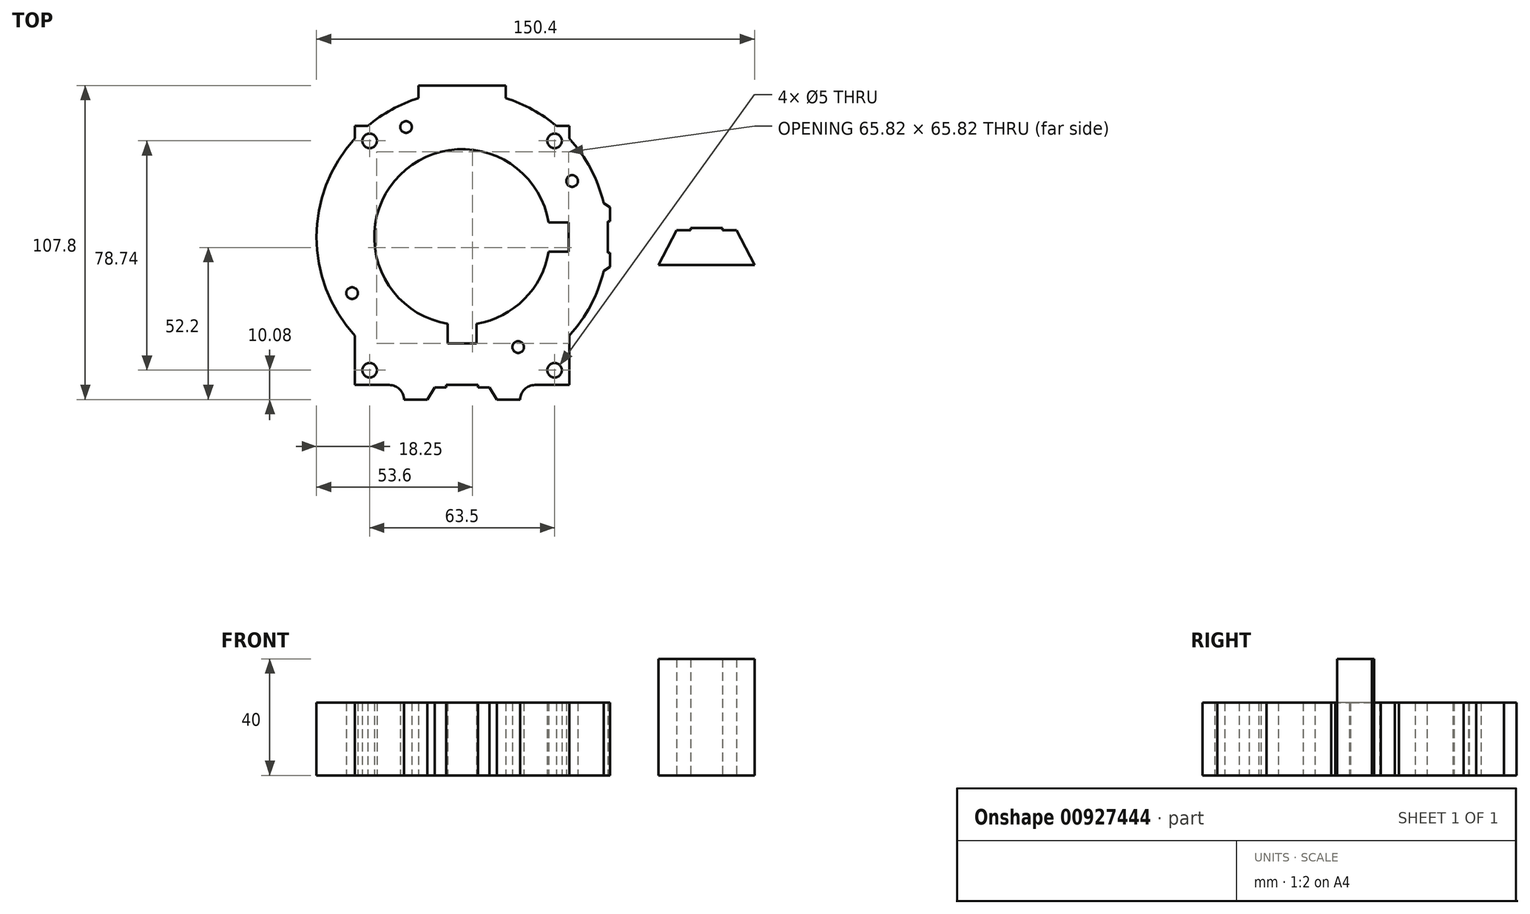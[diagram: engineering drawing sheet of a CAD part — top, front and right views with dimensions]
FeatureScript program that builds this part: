
annotation { "Feature Type Name" : "Feature", "Feature Type Description" : "" }
export const myFeature = defineFeature(function(context is Context, id is Id, definition is map)
    precondition{}
    {
        {
            var Q0;
            Q0=qCreatedBy(makeId("Top.planeOp"),FACE);
            var sketch = newSketch(context, id + "F0", { "sketchPlane" : qUnion([Q0])});
            skArc(sketch, "E0", {"start": v(36.83, -33.82) * mm, "mid": v(44.15, -23.47) * mm, "end": v(48.63, -11.6) * mm});
            skArc(sketch, "E1", {"start": v(5, -29.75) * mm, "mid": v(21.33, -21.33) * mm, "end": v(29.75, -5) * mm});
            skLineSegment(sketch, "E2.bottom", {"start": v(36.83, -50.8) * mm, "end": v(24.97, -50.8) * mm});
            skLineSegment(sketch, "E2.top", {"start": v(36.83, 38.1) * mm, "end": v(32.38, 38.1) * mm});
            skLineSegment(sketch, "E2.right", {"start": v(-36.83, -50.8) * mm, "end": v(-36.83, -33.82) * mm});
            skPoint(sketch, "E2.middle", {"position": v(0, -6.35) * mm});
            skLineSegment(sketch, "E3", {"start": v(0, 0) * mm, "end": v(37.78, 19.25) * mm, "construction": true});
            skCircle(sketch, "E4", {"center": v(37.78, 19.25) * mm, "radius": 2 * mm});
            skLineSegment(sketch, "E5.bottom", {"start": v(-36.83, -50.8) * mm, "end": v(-31.75, -50.8) * mm, "construction": true});
            skLineSegment(sketch, "E5.top", {"start": v(-36.83, -45.72) * mm, "end": v(-31.75, -45.72) * mm, "construction": true});
            skLineSegment(sketch, "E5.left", {"start": v(-36.83, -50.8) * mm, "end": v(-36.83, -45.72) * mm, "construction": true});
            skLineSegment(sketch, "E5.right", {"start": v(-31.75, -50.8) * mm, "end": v(-31.75, -45.72) * mm, "construction": true});
            skLineSegment(sketch, "E6", {"start": v(0, -6.35) * mm, "end": v(11.23, -6.35) * mm, "construction": true});
            skLineSegment(sketch, "E7", {"start": v(36.83, 38.1) * mm, "end": v(36.83, 33.82) * mm});
            skArc(sketch, "E8.trimOffspring", {"start": v(32.38, 38.1) * mm, "mid": v(24.17, 43.77) * mm, "end": v(15, 47.7) * mm});
            skLineSegment(sketch, "E9.trimOffspring", {"start": v(-32.38, 38.1) * mm, "end": v(-36.83, 38.1) * mm});
            skArc(sketch, "E10.trimOffspring", {"start": v(-36.83, 33.82) * mm, "mid": v(-50, 0) * mm, "end": v(-36.83, -33.82) * mm});
            skLineSegment(sketch, "E11.trimOffspring", {"start": v(-36.83, 33.82) * mm, "end": v(-36.83, 38.1) * mm});
            skLineSegment(sketch, "E12", {"start": v(-36.83, 33.82) * mm, "end": v(-36.83, -33.82) * mm, "construction": true});
            skLineSegment(sketch, "E13", {"start": v(36.83, -33.82) * mm, "end": v(36.83, 33.82) * mm, "construction": true});
            skLineSegment(sketch, "E14", {"start": v(32.38, 38.1) * mm, "end": v(-32.38, 38.1) * mm, "construction": true});
            skCircle(sketch, "E15", {"center": v(37.78, 19.25) * mm, "radius": 4 * mm, "construction": true});
            skLineSegment(sketch, "E16", {"start": v(3.2, -36.51) * mm, "end": v(3.2, -50.8) * mm, "construction": true});
            skLineSegment(sketch, "E17.MirrorCS", {"start": v(-3.2, -36.51) * mm, "end": v(-3.2, -50.8) * mm, "construction": true});
            skLineSegment(sketch, "E18", {"start": v(36.83, -50.8) * mm, "end": v(36.83, -33.82) * mm});
            skLineSegment(sketch, "E19", {"start": v(83.9, -9.58) * mm, "end": v(100.4, -9.58) * mm});
            skLineSegment(sketch, "E20", {"start": v(83.9, 3.12) * mm, "end": v(89.35, 3.12) * mm});
            skLineSegment(sketch, "E21", {"start": v(89.35, 3.12) * mm, "end": v(89.35, 2.32) * mm});
            skLineSegment(sketch, "E22", {"start": v(89.35, 2.32) * mm, "end": v(94.18, 2.32) * mm});
            skLineSegment(sketch, "E23", {"start": v(100.4, -9.58) * mm, "end": v(94.18, 2.32) * mm});
            skLineSegment(sketch, "E24.MirrorCS", {"start": v(78.46, 3.12) * mm, "end": v(78.46, 2.32) * mm});
            skLineSegment(sketch, "E25.MirrorCS", {"start": v(78.46, 2.32) * mm, "end": v(73.63, 2.32) * mm});
            skLineSegment(sketch, "E26.MirrorCS", {"start": v(67.4, -9.58) * mm, "end": v(73.63, 2.32) * mm});
            skLineSegment(sketch, "E27.MirrorCS", {"start": v(83.9, -9.58) * mm, "end": v(67.4, -9.58) * mm});
            skLineSegment(sketch, "E28.MirrorCS", {"start": v(83.9, 3.12) * mm, "end": v(78.46, 3.12) * mm});
            skLineSegment(sketch, "E29", {"start": v(0, -50.8) * mm, "end": v(5.44, -50.8) * mm, "construction": true});
            skLineSegment(sketch, "E30", {"start": v(5.44, -50.8) * mm, "end": v(5.44, -51.6) * mm});
            skLineSegment(sketch, "E31", {"start": v(5.44, -51.6) * mm, "end": v(9.45, -51.6) * mm});
            skLineSegment(sketch, "E32", {"start": v(9.45, -51.6) * mm, "end": v(11.97, -55.8) * mm});
            skLineSegment(sketch, "E33", {"start": v(11.97, -55.8) * mm, "end": v(19.97, -55.8) * mm});
            skLineSegment(sketch, "E34", {"start": v(19.97, -55.8) * mm, "end": v(24.97, -55.8) * mm, "construction": true});
            skArc(sketch, "E35", {"start": v(19.97, -55.8) * mm, "mid": v(21.43, -52.26) * mm, "end": v(24.97, -50.8) * mm});
            skLineSegment(sketch, "E36.MirrorCS", {"start": v(-5.44, -50.8) * mm, "end": v(-5.44, -51.6) * mm});
            skLineSegment(sketch, "E37.MirrorCS", {"start": v(-5.44, -51.6) * mm, "end": v(-9.45, -51.6) * mm});
            skLineSegment(sketch, "E38.MirrorCS", {"start": v(-19.97, -55.8) * mm, "end": v(-24.97, -55.8) * mm, "construction": true});
            skLineSegment(sketch, "E39.MirrorCS", {"start": v(-9.45, -51.6) * mm, "end": v(-11.97, -55.8) * mm});
            skArc(sketch, "E40.MirrorCS", {"start": v(-19.97, -55.8) * mm, "mid": v(-21.43, -52.26) * mm, "end": v(-24.97, -50.8) * mm});
            skLineSegment(sketch, "E41.MirrorCS", {"start": v(-11.97, -55.8) * mm, "end": v(-19.97, -55.8) * mm});
            skLineSegment(sketch, "E42.trimOffspring", {"start": v(-24.97, -50.8) * mm, "end": v(-36.83, -50.8) * mm});
            skLineSegment(sketch, "E43.trimOffspring", {"start": v(5.44, -50.8) * mm, "end": v(-5.44, -50.8) * mm});
            skLineSegment(sketch, "E44", {"start": v(-24.97, -50.8) * mm, "end": v(-5.44, -50.8) * mm, "construction": true});
            skLineSegment(sketch, "E45", {"start": v(5.44, -50.8) * mm, "end": v(24.97, -50.8) * mm, "construction": true});
            skLineSegment(sketch, "E46", {"start": v(50, 0) * mm, "end": v(50, 5.45) * mm});
            skLineSegment(sketch, "E47", {"start": v(50, 5.45) * mm, "end": v(50.8, 5.45) * mm});
            skLineSegment(sketch, "E48", {"start": v(50.8, 5.45) * mm, "end": v(50.8, 10.28) * mm});
            skLineSegment(sketch, "E49", {"start": v(50.8, 10.28) * mm, "end": v(48.63, 11.6) * mm});
            skLineSegment(sketch, "E50.MirrorCS", {"start": v(50, 0) * mm, "end": v(50, -5.45) * mm});
            skLineSegment(sketch, "E51.MirrorCS", {"start": v(50, -5.45) * mm, "end": v(50.8, -5.45) * mm});
            skLineSegment(sketch, "E52.MirrorCS", {"start": v(50.8, -5.45) * mm, "end": v(50.8, -10.28) * mm});
            skLineSegment(sketch, "E53.MirrorCS", {"start": v(50.8, -10.28) * mm, "end": v(48.63, -11.6) * mm});
            skArc(sketch, "E54.trimOffspring", {"start": v(48.63, 11.6) * mm, "mid": v(44.15, 23.47) * mm, "end": v(36.83, 33.82) * mm});
            skArc(sketch, "E55", {"start": v(48.63, 11.6) * mm, "mid": v(50, 0) * mm, "end": v(48.63, -11.6) * mm, "construction": true});
            skLineSegment(sketch, "E56", {"start": v(0, 50) * mm, "end": v(0, 52) * mm, "construction": true});
            skLineSegment(sketch, "E57", {"start": v(0, 52) * mm, "end": v(15, 52) * mm});
            skLineSegment(sketch, "E58", {"start": v(15, 52) * mm, "end": v(15, 47.7) * mm});
            skLineSegment(sketch, "E59.MirrorCS", {"start": v(0, 52) * mm, "end": v(-15, 52) * mm});
            skLineSegment(sketch, "E60.MirrorCS", {"start": v(-15, 52) * mm, "end": v(-15, 47.7) * mm});
            skArc(sketch, "E61.trimOffspring", {"start": v(-15, 47.7) * mm, "mid": v(-24.17, 43.77) * mm, "end": v(-32.38, 38.1) * mm});
            skArc(sketch, "E62", {"start": v(-15, 47.7) * mm, "mid": v(0, 50) * mm, "end": v(15, 47.7) * mm, "construction": true});
            skLineSegment(sketch, "E63", {"start": v(0, -36.51) * mm, "end": v(5, -36.51) * mm});
            skLineSegment(sketch, "E64", {"start": v(5, -36.51) * mm, "end": v(5, -29.75) * mm});
            skLineSegment(sketch, "E65.MirrorCS", {"start": v(-5, -36.51) * mm, "end": v(-5, -29.75) * mm});
            skLineSegment(sketch, "E66.MirrorCS", {"start": v(0, -36.51) * mm, "end": v(-5, -36.51) * mm});
            skArc(sketch, "E67.MirrorC", {"start": v(-5, -29.75) * mm, "mid": v(-21.33, 21.33) * mm, "end": v(29.75, 5) * mm});
            skArc(sketch, "E68", {"start": v(-5, -29.75) * mm, "mid": v(0, -30.16) * mm, "end": v(5, -29.75) * mm, "construction": true});
            skLineSegment(sketch, "E69.1.0", {"start": v(36.51, 0) * mm, "end": v(36.51, -5) * mm});
            skLineSegment(sketch, "E69.1.1", {"start": v(36.51, 0) * mm, "end": v(36.51, 5) * mm});
            skLineSegment(sketch, "E69.1.2", {"start": v(36.51, 5) * mm, "end": v(29.75, 5) * mm});
            skLineSegment(sketch, "E69.1.3", {"start": v(36.51, -5) * mm, "end": v(29.75, -5) * mm});
            skArc(sketch, "E70.trimOffspring", {"start": v(29.75, -5) * mm, "mid": v(21.33, -21.33) * mm, "end": v(5, -29.75) * mm});
            skArc(sketch, "E71.trimOffspring", {"start": v(29.75, 5) * mm, "mid": v(-21.33, 21.33) * mm, "end": v(-5, -29.75) * mm, "construction": true});
            skArc(sketch, "E72", {"start": v(29.75, -5) * mm, "mid": v(30.16, 0) * mm, "end": v(29.75, 5) * mm, "construction": true});
            skArc(sketch, "E73", {"start": v(-36.83, -33.82) * mm, "mid": v(0, -50) * mm, "end": v(36.83, -33.82) * mm, "construction": true});
            skCircle(sketch, "E74", {"center": v(-31.75, -45.72) * mm, "radius": 2.5 * mm});
            skCircle(sketch, "E75", {"center": v(-31.75, -45.72) * mm, "radius": 3.2 * mm, "construction": true});
            skCircle(sketch, "E76.MirrorC", {"center": v(31.75, -45.72) * mm, "radius": 3.2 * mm, "construction": true});
            skCircle(sketch, "E77.MirrorC", {"center": v(31.75, -45.72) * mm, "radius": 2.5 * mm});
            skCircle(sketch, "E78.MirrorC", {"center": v(31.75, 33.02) * mm, "radius": 3.2 * mm, "construction": true});
            skCircle(sketch, "E79.MirrorC", {"center": v(31.75, 33.02) * mm, "radius": 2.5 * mm});
            skCircle(sketch, "E80.MirrorC", {"center": v(-31.75, 33.02) * mm, "radius": 3.2 * mm, "construction": true});
            skCircle(sketch, "E81.MirrorC", {"center": v(-31.75, 33.02) * mm, "radius": 2.5 * mm});
            skCircle(sketch, "E82", {"center": v(37.78, 19.25) * mm, "radius": 5 * mm, "construction": true});
            skCircle(sketch, "E83", {"center": v(37.78, 19.25) * mm, "radius": 3.5 * mm, "construction": true});
            skCircle(sketch, "E84.1.0", {"center": v(-19.25, 37.78) * mm, "radius": 2 * mm});
            skCircle(sketch, "E84.1.1", {"center": v(-19.25, 37.78) * mm, "radius": 3.5 * mm, "construction": true});
            skCircle(sketch, "E84.1.2", {"center": v(-19.25, 37.78) * mm, "radius": 4 * mm, "construction": true});
            skCircle(sketch, "E84.1.3", {"center": v(-19.25, 37.78) * mm, "radius": 5 * mm, "construction": true});
            skLineSegment(sketch, "E84.1.4", {"start": v(0, 0) * mm, "end": v(-19.25, 37.78) * mm, "construction": true});
            skCircle(sketch, "E84.2.0", {"center": v(-37.78, -19.25) * mm, "radius": 2 * mm});
            skCircle(sketch, "E84.2.1", {"center": v(-37.78, -19.25) * mm, "radius": 3.5 * mm, "construction": true});
            skCircle(sketch, "E84.2.2", {"center": v(-37.78, -19.25) * mm, "radius": 4 * mm, "construction": true});
            skCircle(sketch, "E84.2.3", {"center": v(-37.78, -19.25) * mm, "radius": 5 * mm, "construction": true});
            skLineSegment(sketch, "E84.2.4", {"start": v(0, 0) * mm, "end": v(-37.78, -19.25) * mm, "construction": true});
            skCircle(sketch, "E84.3.0", {"center": v(19.25, -37.78) * mm, "radius": 2 * mm});
            skCircle(sketch, "E84.3.1", {"center": v(19.25, -37.78) * mm, "radius": 3.5 * mm, "construction": true});
            skCircle(sketch, "E84.3.2", {"center": v(19.25, -37.78) * mm, "radius": 4 * mm, "construction": true});
            skCircle(sketch, "E84.3.3", {"center": v(19.25, -37.78) * mm, "radius": 5 * mm, "construction": true});
            skLineSegment(sketch, "E84.3.4", {"start": v(0, 0) * mm, "end": v(19.25, -37.78) * mm, "construction": true});
            skSolve(sketch);
        }
        {
            var Q0;
            Q0=makeQuery(id+"F0.imprint","IMPRINT",FACE,{"disambiguationData":[TD([[makeQuery(id+"F0.imprint","IMPRINT",EDGE,{"derivedFrom":sQuery(id+"F0.wireOp",EDGE,"E0")}),1.0]])]});
            extrude(context, id + "F1", {"entities" : qUnion([Q0]), "depth" : 25 * mm, "offsetDistance" : 25 * mm});
        }
        {
            var Q0;
            Q0=makeQuery(id+"F0.imprint","IMPRINT",FACE,{"disambiguationData":[TD([[makeQuery(id+"F0.imprint","IMPRINT",EDGE,{"derivedFrom":sQuery(id+"F0.wireOp",EDGE,"E19")}),1.0]])]});
            extrude(context, id + "F2", {"entities" : qUnion([Q0]), "depth" : 40 * mm, "offsetDistance" : 25 * mm});
        }
    });
